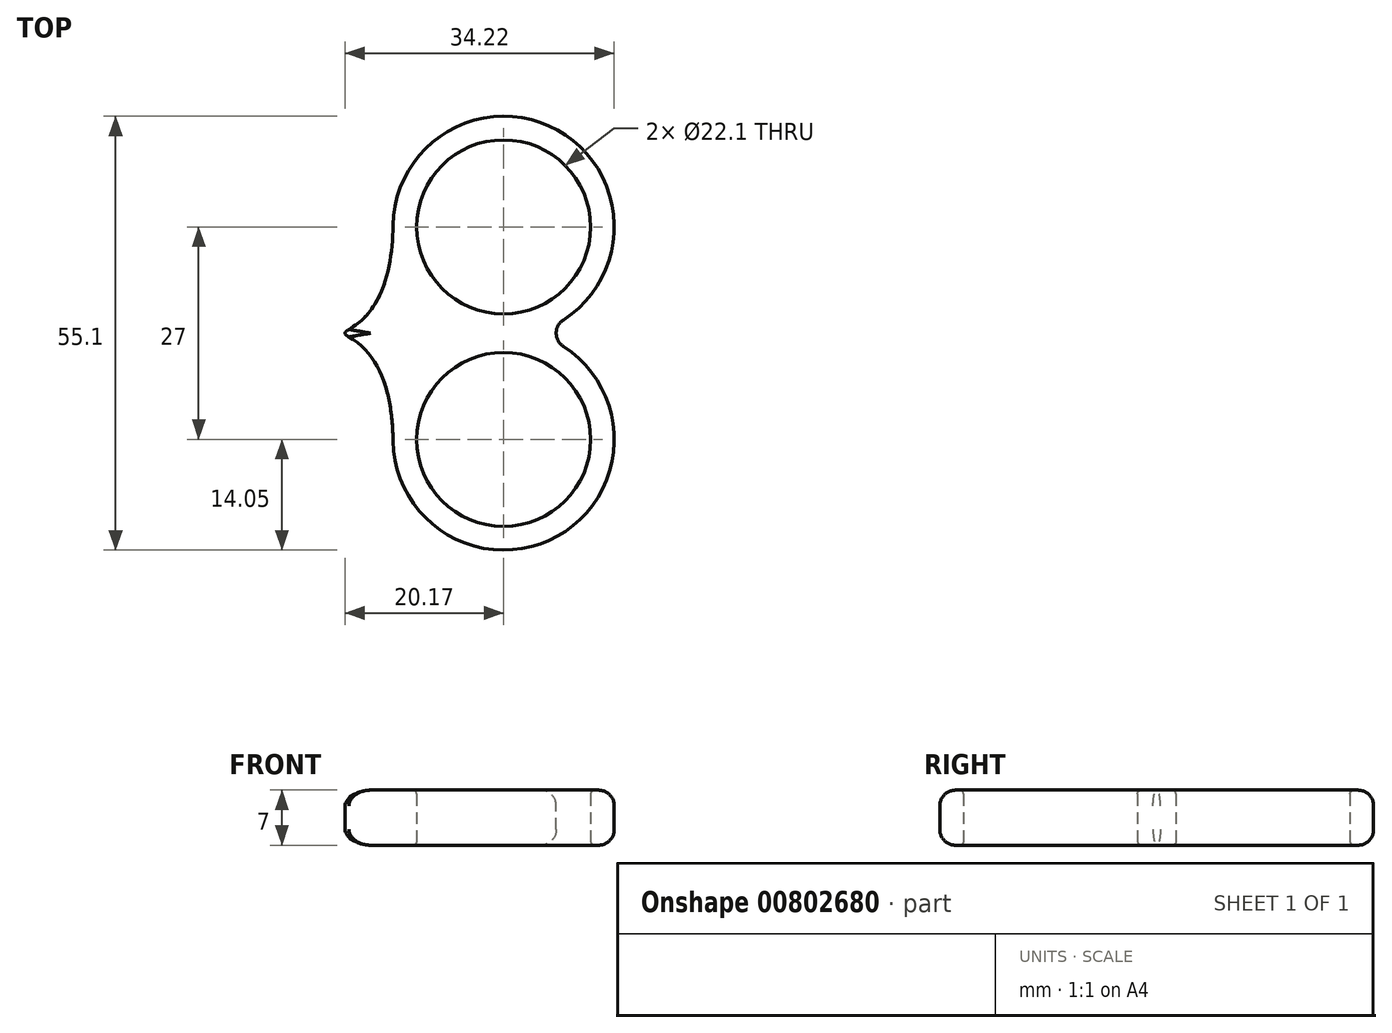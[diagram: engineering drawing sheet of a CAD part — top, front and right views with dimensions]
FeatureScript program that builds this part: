
annotation { "Feature Type Name" : "Feature", "Feature Type Description" : "" }
export const myFeature = defineFeature(function(context is Context, id is Id, definition is map)
    precondition{}
    {
        {
            var Q0;
            Q0=qCreatedBy(makeId("Top.planeOp"),FACE);
            var sketch = newSketch(context, id + "F0", { "sketchPlane" : qUnion([Q0])});
            skCircle(sketch, "E0", {"center": v(0, 0) * mm, "radius": 11.05 * mm});
            skCircle(sketch, "E1.0", {"center": v(0, 0) * mm, "radius": 14.05 * mm});
            skCircle(sketch, "E2", {"center": v(0, 27) * mm, "radius": 11.05 * mm});
            skCircle(sketch, "E3.0", {"center": v(0, 27) * mm, "radius": 14.05 * mm});
            skFitSpline(sketch, "E4", {"points": [v(-14.05, 27.2) * mm, v(-20.17, 13.5) * mm, v(-14.05, -0.2) * mm], "startDerivative": vector(-1.06, -73.32) * mm, "endDerivative": vector(1.06, -73.32) * mm});
            skLineSegment(sketch, "E5", {"start": v(0, 58.81) * mm, "end": v(0, -18.81) * mm, "construction": true});
            skLineSegment(sketch, "E6", {"start": v(-42.72, 13.5) * mm, "end": v(42.72, 13.5) * mm, "construction": true});
            skSolve(sketch);
        }
        {
            var Q0;
            Q0=makeQuery(id+"F0.imprint","IMPRINT",FACE,{"disambiguationData":[TD([[makeQuery(id+"F0.imprint","IMPRINT",EDGE,{"derivedFrom":sQuery(id+"F0.wireOp",EDGE,"E2")}),-1.0]])]});
            var Q1;
            {var subQ0=sQuery(id+"F0.wireOp",EDGE,"22dc2019-c184-4316-87eb-549f702f038a");Q1=makeQuery(id+"F0.imprint","IMPRINT",FACE,{"disambiguationData":[TD([[makeQuery(id+"F0.imprint","IMPRINT",EDGE,{"derivedFrom":subQ0}),1.0]])]});}
            var Q2;
            Q2=makeQuery(id+"F0.imprint","IMPRINT",FACE,{"disambiguationData":[TD([[makeQuery(id+"F0.imprint","IMPRINT",EDGE,{"derivedFrom":sQuery(id+"F0.wireOp",EDGE,"E0")}),-1.0]])]});
            var Q3;
            {var subQ0=sQuery(id+"F0.wireOp",EDGE,"E3.0");var subQ1=sQuery(id+"F0.wireOp",EDGE,"E1.0");var subQ2=makeQuery(id+"F0.imprint","INTERSECT",VERTEX,{"disambiguationData":[OD(0.0)],"derivedFrom":[subQ1,subQ0]});Q3=makeQuery(id+"F0.imprint","IMPRINT",FACE,{"disambiguationData":[TD([[makeQuery(id+"F0.imprint","IMPRINT",EDGE,{"disambiguationData":[TD([[subQ2,-1.0]])],"derivedFrom":subQ1}),1.0]])]});}
            var Q4;
            {var subQ0=sQuery(id+"F0.wireOp",EDGE,"E4");Q4=makeQuery(id+"F0.imprint","IMPRINT",FACE,{"disambiguationData":[TD([[makeQuery(id+"F0.imprint","IMPRINT",EDGE,{"derivedFrom":subQ0}),1.0]])]});}
            extrude(context, id + "F1", {"entities" : qUnion([Q0, Q1, Q2, Q3, Q4]), "depth" : 7 * mm, "offsetDistance" : 25 * mm});
        }
        {
            var Q0;
            Q0=makeQuery(id+"F1.opExtrude","SWEPT_FACE",FACE,{"disambiguationData":[OSD([sQuery(id+"F0.wireOp",EDGE,"E2")])]});
            var Q1;
            Q1=makeQuery(id+"F1.opExtrude","SWEPT_FACE",FACE,{"disambiguationData":[OSD([sQuery(id+"F0.wireOp",EDGE,"E0")])]});
            fillet(context, id + "F2", {"entities" : qUnion([Q0, Q1]), "radius" : .5 * mm, "tangentPropagation" : true, "allowEdgeOverflow" : false});
        }
        {
            var Q0;
            Q0=makeQuery(id+"F1.opExtrude","SWEPT_FACE",FACE,{"disambiguationData":[OSD([sQuery(id+"F0.wireOp",EDGE,"E3.0")])]});
            fillet(context, id + "F3", {"entities" : qUnion([Q0]), "radius" : 2 * mm, "tangentPropagation" : true, "allowEdgeOverflow" : false});
        }
    });
